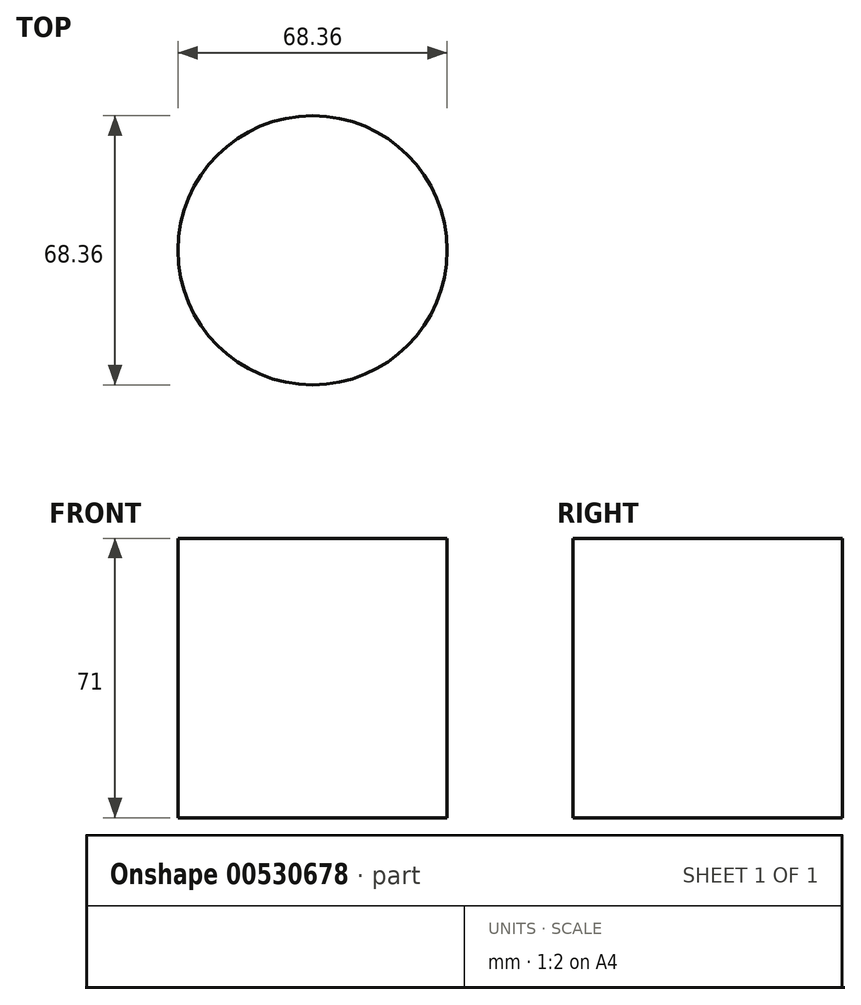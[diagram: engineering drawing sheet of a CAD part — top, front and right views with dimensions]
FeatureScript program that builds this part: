
annotation { "Feature Type Name" : "Feature", "Feature Type Description" : "" }
export const myFeature = defineFeature(function(context is Context, id is Id, definition is map)
    precondition{}
    {
        {
            var Q0;
            Q0=qCreatedBy(makeId("Top.planeOp"),FACE);
            var sketch = newSketch(context, id + "F0", { "sketchPlane" : qUnion([Q0])});
            skCircle(sketch, "E0", {"center": v(0, 0) * mm, "radius": 34.18 * mm});
            skSolve(sketch);
        }
        {
            var Q0;
            Q0=makeQuery(id+"F0.imprint","IMPRINT",FACE,{"disambiguationData":[TD([[makeQuery(id+"F0.imprint","IMPRINT",EDGE,{"derivedFrom":sQuery(id+"F0.wireOp",EDGE,"E0")}),1.0]])]});
            extrude(context, id + "F1", {"entities" : qUnion([Q0]), "depth" : 71 * mm, "offsetDistance" : 25 * mm});
        }
    });
